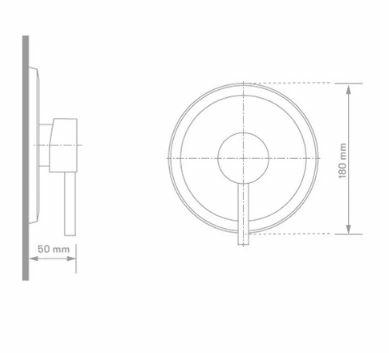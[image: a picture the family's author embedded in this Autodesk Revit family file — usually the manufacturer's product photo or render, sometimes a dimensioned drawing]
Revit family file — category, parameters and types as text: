
# Revit family: 01-2459-11 GANCHO METALICO QUADRA
name_source: partatom
category: Plumbing Fixtures
revit_build: Autodesk Revit 2018 (Build: 20170223_1515(x64)
units: mm (PartAtom-declared; Revit-internal decimal feet)

## family parameters
Cut with Voids When Loaded = No
Host = Face
OmniClass Number = 23.31.11.00
Part Type = Normal
Room Calculation Point = No
Round Connector Dimension = Use Diameter
Shared = No

## types (1)
- 01-2459-11
    Ancho Soporte = 22 mm  [stored 0.0721785 ft]
    Ancho gancho = 71 mm  [stored 0.23294 ft]
    CW Connection = Yes
    Default Elevation = 0 mm  [stored 0 ft]
    Description = GANCHO
    HW Connection = Yes
    Link Ficha Tecnica = http://infotecnica.gricol.com
    Manufacturer = Gricol
    Model = 01-2458-11
    Product Name = GANCHO METALICO QUADRA
    Profundidad = 75 mm  [stored 0.246063 ft]
    Soporte y gancho = Metal Laton Cromado
    Type Image = GANCHO METALICO QUADRA.JPG
    URL = https://www.gricol.com
    Vent Connection = No
    Waste Connection = No

note: [stored X ft] marks values corroborated as IEEE doubles in the binary element streams (Revit-internal decimal feet)

## geometry (parser evidence)
native form markers: Blend x2, Sweep x4
no freeform markers — native parametric forms only
